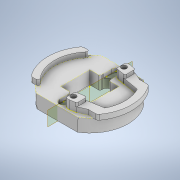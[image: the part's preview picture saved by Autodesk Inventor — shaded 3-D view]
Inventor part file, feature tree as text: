
AUTODESK INVENTOR PART (.ipt)
format: ipt  version: 2020 (Build 240168000, 168)  size: 505,344 bytes
history: native  units: mm
features: projected_geometry x15, sketch x12, extrude x10, fillet x5, other x3, revolve x1
ambient origin geometry x8: Origin, YZ Plane, XZ Plane, XY Plane, X Axis, Y Axis, Z Axis, Center Point
bodies: Body1 (feature_tree)
feature tree (46):
  other  "Твердое тело1"
  extrude  "Выдавливание1"  Depth=17.1mm
  extrude  "Выдавливание2"  Depth=17.1mm
  other  "РабПлоскость1"
  sketch  "Эскиз3"
  other  "РабОсь1"
  revolve  "Вращение1"
  extrude  "Выдавливание3"  Depth=25.0mm
  extrude  "Выдавливание4"  Depth=5.3mm
  extrude  "Выдавливание5"  Depth=44.7mm
  extrude  "Выдавливание6"  Depth=7.7mm TaperAngle=0.0deg
  extrude  "Выдавливание7"  Depth=5.0mm
  extrude  "Выдавливание8"  Depth=30.65mm
  sketch  "Эскиз10"
  extrude  "Выдавливание9"  Depth=2.5mm TaperAngle=0.0deg
  fillet  "Сопряжение1"  Radius=0.2mm
  fillet  "Сопряжение2"  [1 undecoded]
  fillet  "Сопряжение3"  Radius=1.85mm
  extrude  "Выдавливание10"  Depth=30.0mm
  fillet  "Сопряжение4"  Radius=2.0mm
  fillet  "Сопряжение5"  Radius=3.0mm
  sketch  "Эскиз1"
  sketch  "Эскиз2"
  projected_geometry  "Спроецированная петля1"
  projected_geometry  "Спроецированная петля2"
  sketch  "Эскиз4"
  projected_geometry  "Спроецированная петля3"
  sketch  "Эскиз5"
  sketch  "Эскиз6"
  projected_geometry  "Спроецированная петля4"
  sketch  "Эскиз7"
  projected_geometry  "Спроецированная петля5"
  sketch  "Эскиз8"
  projected_geometry  "Спроецированная петля6"
  projected_geometry  "Спроецированная петля7"
  projected_geometry  "Спроецированная петля8"
  sketch  "Эскиз9"
  projected_geometry  "Спроецированная петля9"
  projected_geometry  "Спроецированная петля10"
  projected_geometry  "Спроецированная петля11"
  projected_geometry  "Спроецированная петля12"
  sketch  "Эскиз11"
  sketch  "Эскиз12"
  projected_geometry  "Спроецированная петля13"
  projected_geometry  "Спроецированная петля14"
  projected_geometry  "Спроецированная петля15"
note: 1 required parameter value undecoded (feature->parameter linkage not recoverable at this tier; creation-order binding heuristic only, values carry confidence <= 0.55)
